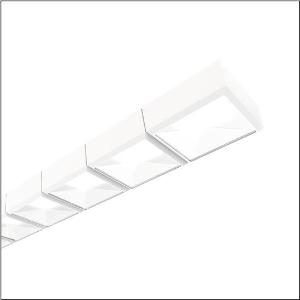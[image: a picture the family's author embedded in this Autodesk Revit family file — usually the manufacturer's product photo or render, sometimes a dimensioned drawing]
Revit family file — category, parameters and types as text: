
# Revit family: scriptus_r__11_5mz312d0twb_510a
name_source: partatom
category: Lighting Fixtures
units: mm (PartAtom-declared; Revit-internal decimal feet)

## family parameters
Cut with Voids When Loaded = No
Host = Face
Light Source = No
Part Type = Normal
Room Calculation Point = No
Round Connector Dimension = Use Diameter
Shared = No

## types (1)
- --- (1 x LED 3000K+6500K / CRI = 80 (unbekannt), 3200 lm / 2380 lm, 3000K)
    Apparent Load = 94 VA
    CIE Flux Codes = 0 0 0 0 100 / 82 95 99 100 100
    Color Rendering = 80
    Color Temperature = 3000K
    Default Elevation = 1800 mm
    Description = Scriptus® 11, office luminaire, primary optical cover: lenses, CAT 2 (L<= 3000cd/m²), light emission: direct/indirect distribution, primary light characteristic: symmetric, installation type: suspended mounting, LED, rated luminous flux: 11.150lm, luminous efficacy: 116lm/W, light colour: 8tw, colour temperature: 3000..6500K, control gear: ECG DALI, with terminal, 5-pole, mains connection: 230V, AC, 50Hz, rated input power: 96W, LED, control gear: ECG DALI, housing, luminaire housing, of aluminium, traffic white (RAL 9016), length: 1.768mm, width: 114mm, height: 57mm, protection rating (complete): IP20, insulation class (complete): insulation class I (protective earthing), certification: CE, protection symbol: F, permissible operating ambient temperature: <= +25°C, standard: EN 50419, packaging unit: 1 piece
    Height = 57 mm
    Lamp = 1 x LED 3000K+6500K / CRI >= 80 (unbekannt)
    Lamp Light Flux = 3200 lm / 2380 lm
    Lamp count = 1
    Length = 1768 mm
    Luminous efficacy = 119 lm/W
    Manufacturer = Siteco
    ModVariant = No
    Model = 5MZ312D0TWB
    Mounting Place = Ceiling
    Mounting Type = Pendant
    Number of Poles = 1
    OnlyDefault = Yes
    Power Factor = 1
    Product Name = Scriptus® 11
    Product group = office luminaire | ceiling pendant
    ProductGroupID = 902
    Protection Class = Protection class I
    Protection Degree = IP 20
    RLX_Detail_Level = 1
    RLX_Emergency_Light_Flux = 0 lm
    RLX_Emergency_Type = 0
    RLX_Emergency_Type_DB = No
    RlxData = <blob elided: 31721 chars, md5=80881264>
    Socket = socket
    Standby Power = 0 W
    System Light Flux = 11160 lm
    System Power = 94 W
    Type Comments = individual setting: colour temperature 6500K
    Type Image = l_1004839.jpg
    URL = http://relux.com
    VarID = @adj_148960
    Voltage = 0 V
    Weight = 0.00 kg
    Width = 114 mm

## geometry (parser evidence)
native form markers: Blend x4, Sweep x17
no freeform markers — native parametric forms only
